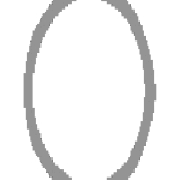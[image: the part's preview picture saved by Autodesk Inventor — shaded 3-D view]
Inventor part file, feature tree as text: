
AUTODESK INVENTOR PART (.ipt)
format: ipt  version: 2021 (Build 250183000, 183)  size: 109,568 bytes
history: native  units: in
note: dims shown in document units (in); Inventor stores cm internally (conversion verified against a paired STEP export)
features: other x4, sketch x3, plane x1
ambient origin geometry x8: Origin, YZ Plane, XZ Plane, XY Plane, X Axis, Y Axis, Z Axis, Center Point
bodies: Solid1 (feature_tree), Body (feature_tree)
feature tree (8):
  other  "Driven Length"
  other  "Frame Generator"
  other  "Start Plane"
  other  "End Plane"
  sketch  "Sketch"  dims[d2=14.625in d4=-0.0in d5=14.625in d6=0.12in d7=0.0in d8=90.0deg d9=14.625in]
  sketch  "Sketch2"  dims[d0=1.0in]
  plane  "Work Plane3"
  sketch  "Sketch3"  dims[d1=0.065in]
